# Revit family: 0042225
name_source: partatom
category: Lighting Fixtures
revit_build: Autodesk Revit 2017 (Build: 20190507_1515(x64)
units: mm (PartAtom-declared; Revit-internal decimal feet)

## family parameters
Cut with Voids When Loaded = No
Host = Face
Light Source = Yes
OmniClass Number = 23.80.70.00
OmniClass Title = Lighting
Part Type = Normal
Room Calculation Point = No
Round Connector Dimension = Use Diameter
Shared = No

## types (9) — shared parameters
-BOX_WIDTH_SYL = -40 mm
-LUMDEPTH_SYL = -127 mm
Assembly Code = D5020200
AssetType = Fixed
BOX_WIDTH_SYL = 40 mm  [stored 0.131234 ft]
ClassificationName = Uniclass2015
ClassificationValue = EF_70_80
Color Filter = 16777215
DEPTH_SYL = 598 mm
Default Elevation = 1219 mm
Dimming Lamp Color Temperature Shift = <None>
DocumentationLiterature = http://www.sylvania-lighting.com
ElectricShockClassification = Class II
Emit Shape Visible in Rendering = No
Emit from Circle Diameter = 610 mm
HEIGHTBOTT_SYL = 7 mm  [stored 0.0229659 ft]
HEIGHT_SYL = 33 mm  [stored 0.108268 ft]
IfcExportAs = IfcLightFixtureType
IfcExportType = IfcLightFixtureType
ImpactProtectionIndex = IK03
IngressProtection = IP40/20
Keynote = 16500
LUMDEPTH_SYL = 127 mm
LUMWIDTH_SYL = 577 mm
Lamp = LED
LampColourRenderingIndex = 80
LampsType = LED
MAINHEIGHT_SYL = 63 mm
Manufacturer = Feilo Sylvania
ManufacturerName = Feilo Sylvania
Material = aluminium,steel housing, other diffuser
Material_1_SYL = <By Category>
Material_2_SYL = <By Category>
Material_3_SYL = <By Category>
Material_4_SYL = <By Category>
NominalDepth = 295 mm  [stored 0.967848 ft]
NominalLength = 1195 mm  [stored 3.9206 ft]
PowerFactor = 0.9
TOP_DEPTH_SYL = 95 mm
TOP_WIDTH_SYL = 265 mm  [stored 0.869423 ft]
TOP__WIDTH_SYL = 545 mm
Tilt Angle = -90.00°
Type Image = <None>
URL = http://www.sylvania-lighting.com
Voltage = 0 V
WIDTH_SYL = 148 mm
zero-valued in all types: Cost

## per-type parameters (varying)
| type | Apparent Load | LampColourTemperature | LampMacAdamStep | LampNominalLuminous | LuminousEfficacy | Model | ModelNumber | ModelReference | Name | NominalHeight | Photometric Web File | PowerConsumption | TypeName |
| 0042254 ST PANEL 1200X300HE DALI 4100LM 865 | 34 VA | 6500 K | 6 | 4100 lm | 121 lm/W | START Panel 1200x300HE DALI 4100Lm 865 | 0042254 | START Panel 1200x300HE DALI 4100Lm 865 | START Panel 1200x300HE DALI 4100Lm 865 | 34 mm | 0042254.ies | 34 W | START Panel 1200x300HE DALI 4100Lm 865 |
| 0042253 ST PANEL 1200X300HE DALI 4100LM 840 | 34 VA | 4000 K | 3 | 4100 lm | 121 lm/W | START Panel 1200x300HE DALI 4100Lm 840 | 0042253 | START Panel 1200x300HE DALI 4100Lm 840 | START Panel 1200x300HE DALI 4100Lm 840 | 34 mm | 0042253.ies | 34 W | START Panel 1200x300HE DALI 4100Lm 840 |
| 0042252 ST PANEL 1200X300HE DALI 3900LM 830 | 34 VA | 3000 K | 3 | 3900 lm | 115 lm/W | START Panel 1200x300HE DALI 3900Lm 830 | 0042252 | START Panel 1200x300HE DALI 3900Lm 830 | START Panel 1200x300HE DALI 3900Lm 830 | 34 mm | 0042252.ies | 34 W | START Panel 1200x300HE DALI 3900Lm 830 |
| 0042227 ST PANEL UGR19 1200X300 DALI 3800LM 865 | 36 VA | 6500 K | 6 | 3800 lm | 106 lm/W | START Panel UGR19 1200x300 DALI 3800Lm 865 | 0042227 | START Panel UGR19 1200x300 DALI 3800Lm 865 | START Panel UGR19 1200x300 DALI 3800Lm 865 | 35 mm | 0042227.ies | 36 W | START Panel UGR19 1200x300 DALI 3800Lm 865 |
| 0042226 ST PANEL UGR19 1200X300 DALI 3800LM 840 | 36 VA | 4000 K | 3 | 3800 lm | 106 lm/W | START Panel UGR19 1200x300 DALI 3800Lm 840 | 0042226 | START Panel UGR19 1200x300 DALI 3800Lm 840 | START Panel UGR19 1200x300 DALI 3800Lm 840 | 35 mm | 0042226.ies | 36 W | START Panel UGR19 1200x300 DALI 3800Lm 840 |
| 0042225 ST PANEL UGR19 1200X300 DALI 3600LM 830 | 36 VA | 3000 K | 3 | 3600 lm | 100 lm/W | START Panel UGR19 1200x300 DALI 3600Lm 830 | 0042225 | START Panel UGR19 1200x300 DALI 3600Lm 830 | START Panel UGR19 1200x300 DALI 3600Lm 830 | 35 mm | 0042225.ies | 36 W | START Panel UGR19 1200x300 DALI 3600Lm 830 |
| 0042224 ST PANEL UGR19 1200X300 DALI 3400LM 865 | 36 VA | 6500 K | 6 | 3400 lm | 94 lm/W | START Panel UGR19 1200x300 DALI 3400Lm 865 | 0042224 | START Panel UGR19 1200x300 DALI 3400Lm 865 | START Panel UGR19 1200x300 DALI 3400Lm 865 | 35 mm | 0042224.ies | 36 W | START Panel UGR19 1200x300 DALI 3400Lm 865 |
| 0042223 ST PANEL UGR19 1200X300 DALI 3400LM 840 | 36 VA | 4000 K | 3 | 3400 lm | 94 lm/W | START Panel UGR19 1200x300 DALI 3400Lm 840 | 0042223 | START Panel UGR19 1200x300 DALI 3400Lm 840 | START Panel UGR19 1200x300 DALI 3400Lm 840 | 35 mm | 0042223.ies | 36 W | START Panel UGR19 1200x300 DALI 3400Lm 840 |
| 0042222 ST PANEL UGR19 1200X300 DALI 3200LM 830 | 36 VA | 3000 K | 3 | 3200 lm | 89 lm/W | START Panel UGR19 1200x300 DALI 3200Lm 830 | 0042222 | START Panel UGR19 1200x300 DALI 3200Lm 830 | START Panel UGR19 1200x300 DALI 3200Lm 830 | 35 mm | 0042222.ies | 36 W | START Panel UGR19 1200x300 DALI 3200Lm 830 |

note: [stored X ft] marks values corroborated as IEEE doubles in the binary element streams (Revit-internal decimal feet)

## geometry (parser evidence)
native form markers: Sweep x3
no freeform markers — native parametric forms only
